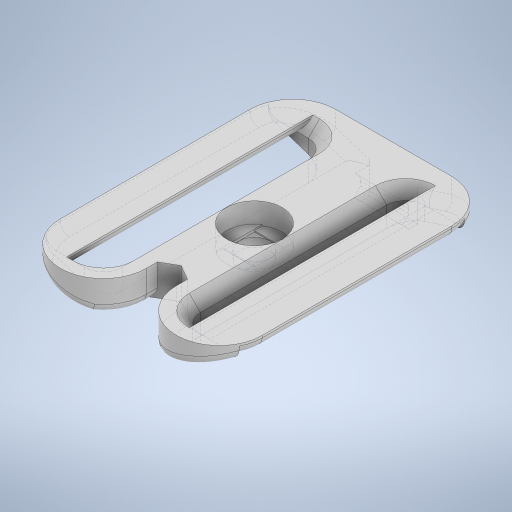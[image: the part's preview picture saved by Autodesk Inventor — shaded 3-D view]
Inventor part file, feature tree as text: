
AUTODESK INVENTOR PART (.ipt)
format: ipt  version: 2024 (Build 280153000, 153)  size: 662,528 bytes
history: native  units: in
note: dims shown in document units (in); Inventor stores cm internally (conversion verified against a paired STEP export)
features: extrude x8, chamfer x3, direct_edit x2, fillet x2, move_body x2, sketch x1
ambient origin geometry x8: Origin, YZ Plane, XZ Plane, XY Plane, X Axis, Y Axis, Z Axis, Center Point
bodies: Solid1 (feature_tree)
feature tree (18):
  sketch  "Sketch1"  dims[d2=0.1181in d3=0.0in d5=0.2677in d6=2.2146in d7=0.785in d8=0.4862in d20=0.1575in d21=0.1575in d27=0.1969in d30=0.1575in d31=0.0in d37=0.3051in d38=0.3051in d44=0.0in d45=0.0in d46=0.0in d47=0.0in d48=-0.0591in d49=0.0591in d50=0.0in d51=0.0in d52=0.0in d53=0.0in d54=-0.0197in d56=0.0591in d57=0.0118in d58=0.0in d59=0.0236in d60=0.0in d61=0.0984in d62=0.0787in d63=45.0deg d64=0.0787in d65=0.2126in d67=0.1181in d68=0.3543in d69=0.0in d73=0.0492in d74=0.0787in d75=45.0deg d76=0.0787in d79=0.0394in d86=0.1181in d87=0.0591in d88=0.0in d89=0.0591in d90=0.0787in d91=45.0deg d92=0.689in d93=0.1654in d97=0.9843in d98=0.1772in d26=0.0197in d28=0.0197in d29=0.0344in d41=0.0197in d42=0.0344in d43=0.0197in d70=0.0197in d71=0.0344in]
  extrude  "Extrusion1"  Depth=0.0787in
  extrude  "Extrusion5"  Depth=0.0787in
  extrude  "Extrusion7"  Depth=0.0787in
  direct_edit  "Direct Edit2"
  extrude  "Extrusion8"  Depth=0.0787in
  direct_edit  "Direct Edit3"
  extrude  "Extrusion9"  Depth=0.0787in
  extrude  "Extrusion10"  Depth=0.0787in
  chamfer  "Chamfer2"  Distance=0.1969in
  fillet  "Fillet1"  Radius=0.1575in
  extrude  "Extrusion11"  Depth=0.0787in
  chamfer  "Chamfer4"  Distance=0.3051in
  fillet  "Fillet2"  [1 undecoded]
  extrude  "Extrusion13"  TaperAngle=0.0deg  [1 undecoded]
  chamfer  "Chamfer5"  Distance=0.0591in
  move_body  "Move2"
  move_body  "Move3"
note: 2 required parameter values undecoded (feature->parameter linkage not recoverable at this tier; creation-order binding heuristic only, values carry confidence <= 0.55)
